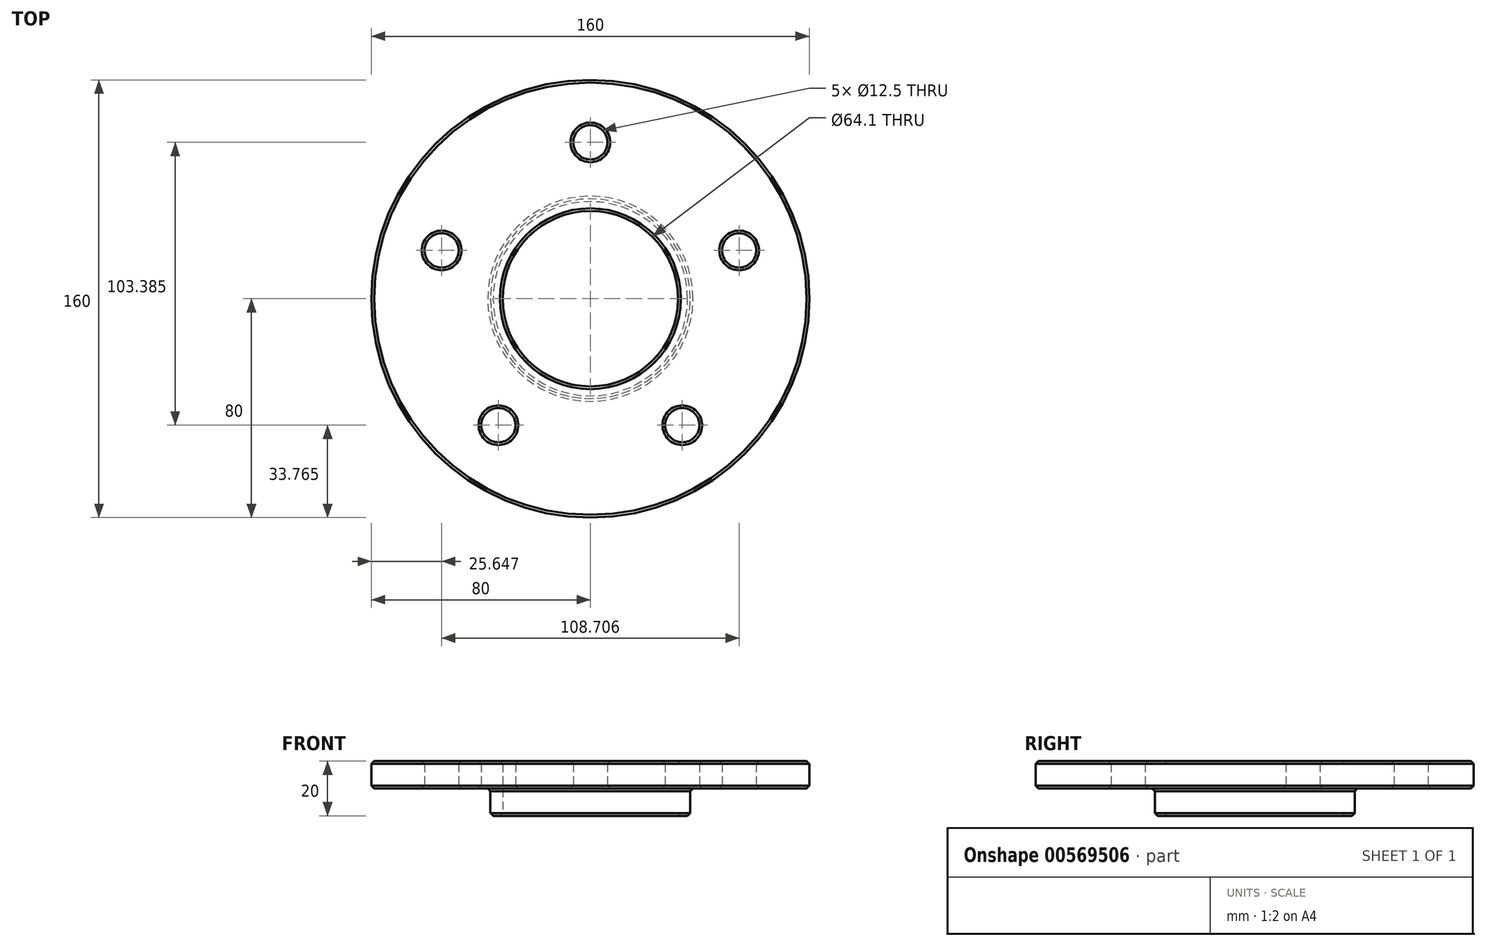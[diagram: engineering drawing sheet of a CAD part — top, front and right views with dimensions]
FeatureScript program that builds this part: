
annotation { "Feature Type Name" : "Feature", "Feature Type Description" : "" }
export const myFeature = defineFeature(function(context is Context, id is Id, definition is map)
    precondition{}
    {
        {
            var Q0;
            Q0=qCreatedBy(makeId("Top.planeOp"),FACE);
            var sketch = newSketch(context, id + "F0", { "sketchPlane" : qUnion([Q0])});
            skCircle(sketch, "E0", {"center": v(0, 0) * mm, "radius": 32.05 * mm});
            skCircle(sketch, "E1", {"center": v(0, 0) * mm, "radius": 57.15 * mm, "construction": true});
            skCircle(sketch, "E2", {"center": v(0, 57.15) * mm, "radius": 6.25 * mm});
            skCircle(sketch, "E3.1.0", {"center": v(-54.35, 17.66) * mm, "radius": 6.25 * mm});
            skCircle(sketch, "E3.2.0", {"center": v(-33.6, -46.24) * mm, "radius": 6.25 * mm});
            skCircle(sketch, "E3.3.0", {"center": v(33.6, -46.24) * mm, "radius": 6.25 * mm});
            skCircle(sketch, "E3.4.0", {"center": v(54.35, 17.66) * mm, "radius": 6.25 * mm});
            skCircle(sketch, "E4", {"center": v(0, 0) * mm, "radius": 80 * mm});
            skLineSegment(sketch, "E5", {"start": v(0, 0) * mm, "end": v(-33.6, -46.24) * mm, "construction": true});
            skLineSegment(sketch, "E6", {"start": v(-33.6, -46.24) * mm, "end": v(-47.02, -64.72) * mm, "construction": true});
            skSolve(sketch);
        }
        {
            var Q0;
            Q0=makeQuery(id+"F0.imprint","IMPRINT",FACE,{"disambiguationData":[TD([[makeQuery(id+"F0.imprint","IMPRINT",EDGE,{"derivedFrom":sQuery(id+"F0.wireOp",EDGE,"E0")}),-1.0]])]});
            extrude(context, id + "F1", {"entities" : qUnion([Q0]), "flatOperationType" : FlatOperationType.REMOVE, "depth" : 10 * mm, "offsetDistance" : 25 * mm, "domain" : OperationDomain.MODEL});
        }
        {
            var Q0;
            Q0=makeQuery(id+"F1.opExtrude","CAP_FACE",FACE,{"disambiguationData":[OSD([sQuery(id+"F0.wireOp",EDGE,"E0"),sQuery(id+"F0.wireOp",EDGE,"E2"),sQuery(id+"F0.wireOp",EDGE,"E3.1.0"),sQuery(id+"F0.wireOp",EDGE,"E3.2.0"),sQuery(id+"F0.wireOp",EDGE,"E3.3.0"),sQuery(id+"F0.wireOp",EDGE,"E3.4.0"),sQuery(id+"F0.wireOp",EDGE,"E4")])],"isStart":false});
            chamfer(context, id + "F2", {"entities" : qUnion([Q0]), "width" : 1 * mm, "tangentPropagation" : true});
        }
        {
            var Q0;
            Q0=makeQuery(id+"F1.opExtrude","CAP_FACE",FACE,{"disambiguationData":[OSD([sQuery(id+"F0.wireOp",EDGE,"E0"),sQuery(id+"F0.wireOp",EDGE,"E2"),sQuery(id+"F0.wireOp",EDGE,"E3.1.0"),sQuery(id+"F0.wireOp",EDGE,"E3.2.0"),sQuery(id+"F0.wireOp",EDGE,"E3.3.0"),sQuery(id+"F0.wireOp",EDGE,"E3.4.0"),sQuery(id+"F0.wireOp",EDGE,"E4"),sQuery(id+"F0.wireOp",EDGE,"DVCKOWd8-CYKK-deTx-SCZA-kz12AxWwtPB0"),sQuery(id+"F0.wireOp",EDGE,"24d471f1-c0f8-4bde-b589-3c8544e44f40.1.0"),sQuery(id+"F0.wireOp",EDGE,"24d471f1-c0f8-4bde-b589-3c8544e44f40.2.0"),sQuery(id+"F0.wireOp",EDGE,"24d471f1-c0f8-4bde-b589-3c8544e44f40.3.0"),sQuery(id+"F0.wireOp",EDGE,"24d471f1-c0f8-4bde-b589-3c8544e44f40.4.0")])],"isStart":true});
            var sketch = newSketch(context, id + "F3", { "sketchPlane" : qUnion([Q0])});
            skCircle(sketch, "E7", {"center": v(0, 0) * mm, "radius": 36.5 * mm});
            skSolve(sketch);
        }
        {
            var Q0;
            Q0=makeQuery(id+"F3.imprint","IMPRINT",FACE,{"disambiguationData":[TD([[makeQuery(id+"F3.imprint","IMPRINT",EDGE,{"derivedFrom":sQuery(id+"F3.wireOp",EDGE,"E7")}),1.0]])]});
            extrude(context, id + "F4", {"entities" : qUnion([Q0]), "operationType" : NewBodyOperationType.ADD, "depth" : 10 * mm, "offsetDistance" : 25 * mm});
        }
        {
            var Q0;
            Q0=makeQuery(id+"F4.opExtrude","CAP_FACE",FACE,{"disambiguationData":[OSD([sQuery(id+"F0.wireOp",EDGE,"E0"),sQuery(id+"F3.wireOp",EDGE,"E7")])],"isStart":false});
            chamfer(context, id + "F5", {"entities" : qUnion([Q0]), "width" : 1 * mm, "tangentPropagation" : true});
        }
        {
            var Q0;
            Q0=makeQuery(id+"F1.opExtrude","CAP_FACE",FACE,{"disambiguationData":[OSD([sQuery(id+"F0.wireOp",EDGE,"E0"),sQuery(id+"F0.wireOp",EDGE,"E2"),sQuery(id+"F0.wireOp",EDGE,"E3.1.0"),sQuery(id+"F0.wireOp",EDGE,"E3.2.0"),sQuery(id+"F0.wireOp",EDGE,"E3.3.0"),sQuery(id+"F0.wireOp",EDGE,"E3.4.0"),sQuery(id+"F0.wireOp",EDGE,"E4"),sQuery(id+"F0.wireOp",EDGE,"DVCKOWd8-CYKK-deTx-SCZA-kz12AxWwtPB0"),sQuery(id+"F0.wireOp",EDGE,"24d471f1-c0f8-4bde-b589-3c8544e44f40.1.0"),sQuery(id+"F0.wireOp",EDGE,"24d471f1-c0f8-4bde-b589-3c8544e44f40.2.0"),sQuery(id+"F0.wireOp",EDGE,"24d471f1-c0f8-4bde-b589-3c8544e44f40.3.0"),sQuery(id+"F0.wireOp",EDGE,"24d471f1-c0f8-4bde-b589-3c8544e44f40.4.0")])],"isStart":true});
            chamfer(context, id + "F6", {"entities" : qUnion([Q0]), "width" : 1 * mm, "tangentPropagation" : true});
        }
    });
